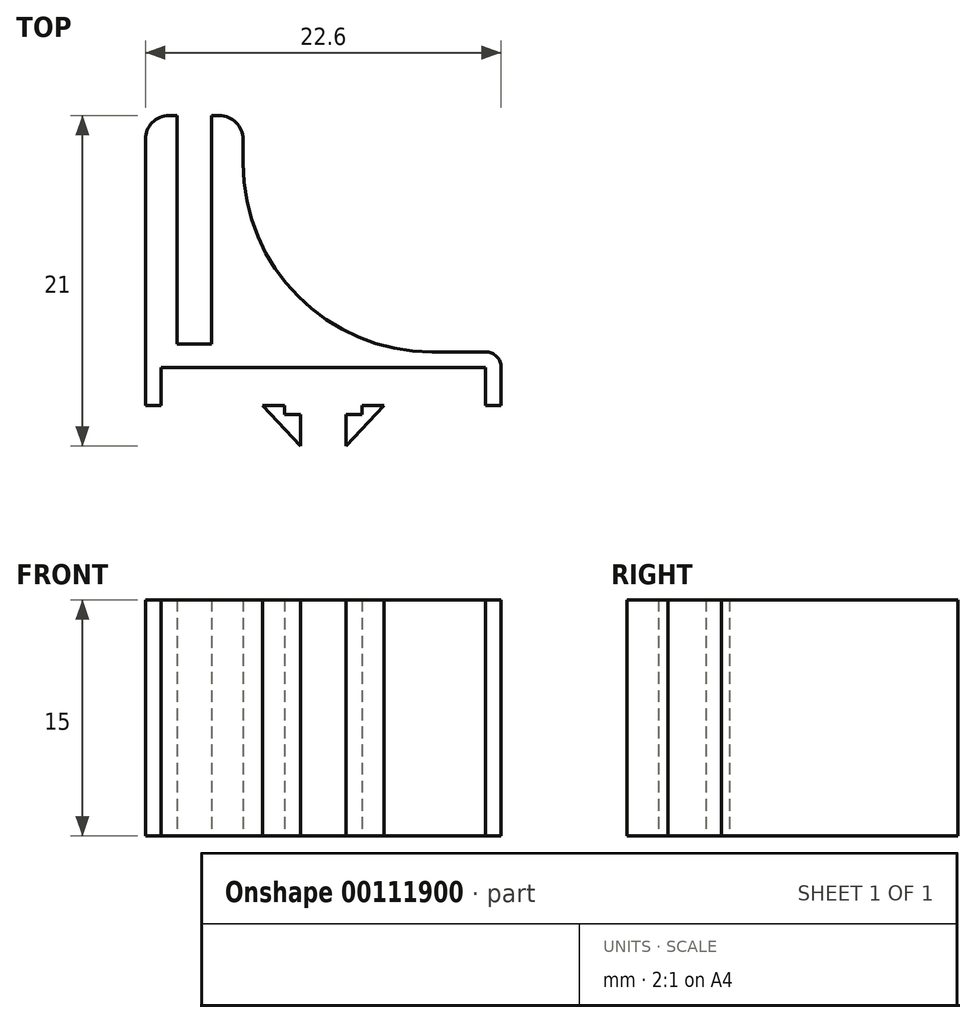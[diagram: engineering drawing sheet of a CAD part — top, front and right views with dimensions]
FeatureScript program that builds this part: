
annotation { "Feature Type Name" : "Feature", "Feature Type Description" : "" }
export const myFeature = defineFeature(function(context is Context, id is Id, definition is map)
    precondition{}
    {
        {
            var Q0;
            Q0=qCreatedBy(makeId("Top.planeOp"),FACE);
            var sketch = newSketch(context, id + "F0", { "sketchPlane" : qUnion([Q0])});
            skLineSegment(sketch, "E0.bottom", {"start": v(-10.3, -5.5) * mm, "end": v(10.3, -5.5) * mm});
            skLineSegment(sketch, "E0.right", {"start": v(10.3, -5.5) * mm, "end": v(10.3, -4.5) * mm});
            skLineSegment(sketch, "E1.bottom", {"start": v(10.3, -5.5) * mm, "end": v(11.3, -5.5) * mm});
            skLineSegment(sketch, "E1.top", {"start": v(10.3, -7.9) * mm, "end": v(11.3, -7.9) * mm});
            skLineSegment(sketch, "E1.left", {"start": v(10.3, -5.5) * mm, "end": v(10.3, -7.9) * mm});
            skLineSegment(sketch, "E1.right", {"start": v(11.3, -5.5) * mm, "end": v(11.3, -7.9) * mm});
            skArc(sketch, "E2", {"start": v(11.3, -5.5) * mm, "mid": v(11, -4.8) * mm, "end": v(10.3, -4.5) * mm});
            skLineSegment(sketch, "E3.bottom", {"start": v(-10.3, -5.5) * mm, "end": v(-11.3, -5.5) * mm});
            skLineSegment(sketch, "E3.top", {"start": v(-10.3, -7.9) * mm, "end": v(-11.3, -7.9) * mm});
            skLineSegment(sketch, "E3.left", {"start": v(-10.3, -5.5) * mm, "end": v(-10.3, -7.9) * mm});
            skLineSegment(sketch, "E3.right", {"start": v(-11.3, -5.5) * mm, "end": v(-11.3, -7.9) * mm});
            skLineSegment(sketch, "E4", {"start": v(-2.45, -5.5) * mm, "end": v(2.45, -5.5) * mm, "construction": true});
            skLineSegment(sketch, "E5.bottom", {"start": v(-2.45, -5.5) * mm, "end": v(-1.45, -5.5) * mm});
            skLineSegment(sketch, "E5.top", {"start": v(-2.45, -8.5) * mm, "end": v(-1.45, -8.5) * mm});
            skLineSegment(sketch, "E5.left", {"start": v(-2.45, -5.5) * mm, "end": v(-2.45, -8.5) * mm});
            skLineSegment(sketch, "E5.right", {"start": v(-1.45, -5.5) * mm, "end": v(-1.45, -8.5) * mm});
            skLineSegment(sketch, "E6.bottom", {"start": v(2.45, -5.5) * mm, "end": v(1.45, -5.5) * mm});
            skLineSegment(sketch, "E6.top", {"start": v(2.45, -8.5) * mm, "end": v(1.45, -8.5) * mm});
            skLineSegment(sketch, "E6.left", {"start": v(2.45, -5.5) * mm, "end": v(2.45, -8.5) * mm});
            skLineSegment(sketch, "E6.right", {"start": v(1.45, -5.5) * mm, "end": v(1.45, -8.5) * mm});
            skLineSegment(sketch, "E7", {"start": v(3.85, -7.9) * mm, "end": v(2.45, -7.9) * mm});
            skLineSegment(sketch, "E8", {"start": v(-2.45, -7.9) * mm, "end": v(-3.85, -7.9) * mm});
            skLineSegment(sketch, "E9", {"start": v(-2.45, -7.9) * mm, "end": v(2.45, -7.9) * mm, "construction": true});
            skLineSegment(sketch, "E10", {"start": v(1.45, -8.5) * mm, "end": v(1.45, -10.5) * mm});
            skLineSegment(sketch, "E11", {"start": v(1.45, -10.5) * mm, "end": v(3.85, -7.9) * mm});
            skLineSegment(sketch, "E12", {"start": v(-1.45, -8.5) * mm, "end": v(-1.45, -10.5) * mm});
            skLineSegment(sketch, "E13", {"start": v(-1.45, -10.5) * mm, "end": v(-3.85, -7.9) * mm});
            skLineSegment(sketch, "E14", {"start": v(-9.3, -4) * mm, "end": v(-7.1, -4) * mm});
            skLineSegment(sketch, "E15", {"start": v(6.9, -4.5) * mm, "end": v(10.3, -4.5) * mm});
            skLineSegment(sketch, "E16", {"start": v(-11.3, -5.5) * mm, "end": v(-11.3, 9) * mm});
            skLineSegment(sketch, "E17", {"start": v(-9.3, -4) * mm, "end": v(-9.3, 10.5) * mm});
            skLineSegment(sketch, "E18", {"start": v(-9.3, 10.5) * mm, "end": v(-9.8, 10.5) * mm});
            skLineSegment(sketch, "E19", {"start": v(-7.1, -4) * mm, "end": v(-7.1, 10.5) * mm});
            skLineSegment(sketch, "E20", {"start": v(-5.1, 7.5) * mm, "end": v(-5.1, 9) * mm});
            skLineSegment(sketch, "E21", {"start": v(-6.6, 10.5) * mm, "end": v(-7.1, 10.5) * mm});
            skLineSegment(sketch, "E22", {"start": v(-9.3, 10.5) * mm, "end": v(-7.1, 10.5) * mm, "construction": true});
            skPoint(sketch, "E23.visualSharp", {"position": v(-11.3, -5.5) * mm});
            skPoint(sketch, "E24.visualSharp", {"position": v(-5.1, -4.5) * mm});
            skArc(sketch, "E24.filletArc", {"start": v(-5.1, 7.5) * mm, "mid": v(-1.59, -0.99) * mm, "end": v(6.9, -4.5) * mm});
            skPoint(sketch, "E25.visualSharp", {"position": v(-11.3, 10.5) * mm});
            skArc(sketch, "E25.filletArc", {"start": v(-9.8, 10.5) * mm, "mid": v(-10.86, 10.06) * mm, "end": v(-11.3, 9) * mm});
            skPoint(sketch, "E26.visualSharp", {"position": v(-5.1, 10.5) * mm});
            skArc(sketch, "E26.filletArc", {"start": v(-5.1, 9) * mm, "mid": v(-5.54, 10.06) * mm, "end": v(-6.6, 10.5) * mm});
            skPoint(sketch, "E27", {"position": v(0, -7.9) * mm});
            skSolve(sketch);
        }
        {
            var Q0;
            Q0=makeQuery(id+"F0.imprint","IMPRINT",FACE,{"disambiguationData":[TD([[makeQuery(id+"F0.imprint","IMPRINT",EDGE,{"derivedFrom":sQuery(id+"F0.wireOp",EDGE,"E1.bottom")}),-1.0]])]});
            var Q1;
            Q1=makeQuery(id+"F0.imprint","IMPRINT",FACE,{"disambiguationData":[TD([[makeQuery(id+"F0.imprint","IMPRINT",EDGE,{"derivedFrom":sQuery(id+"F0.wireOp",EDGE,"E3.bottom")}),1.0]])]});
            var Q2;
            {var subQ1=sQuery(id+"F0.wireOp",EDGE,"E8");Q2=makeQuery(id+"F0.imprint","IMPRINT",FACE,{"disambiguationData":[TD([[makeQuery(id+"F0.imprint","IMPRINT",EDGE,{"derivedFrom":subQ1}),1.0]])]});}
            var Q3;
            {var subQ1=sQuery(id+"F0.wireOp",EDGE,"7c9eb7b9-ca48-4d36-bab2-391d59fa54ff");Q3=makeQuery(id+"F0.imprint","IMPRINT",FACE,{"disambiguationData":[TD([[makeQuery(id+"F0.imprint","IMPRINT",EDGE,{"derivedFrom":subQ1}),-1.0]])]});}
            var Q4;
            Q4=makeQuery(id+"F0.imprint","IMPRINT",FACE,{"disambiguationData":[TD([[makeQuery(id+"F0.imprint","IMPRINT",EDGE,{"derivedFrom":sQuery(id+"F0.wireOp",EDGE,"E0.left")}),1.0]])]});
            var Q5;
            Q5=makeQuery(id+"F0.imprint","IMPRINT",FACE,{"disambiguationData":[TD([[makeQuery(id+"F0.imprint","IMPRINT",EDGE,{"derivedFrom":sQuery(id+"F0.wireOp",EDGE,"E0.right")}),-1.0]])]});
            var Q6;
            {var subQ3=sQuery(id+"F0.wireOp",EDGE,"E5.bottom");Q6=makeQuery(id+"F0.imprint","IMPRINT",FACE,{"disambiguationData":[TD([[makeQuery(id+"F0.imprint","IMPRINT",EDGE,{"derivedFrom":subQ3}),-1.0]])]});}
            var Q7;
            {var subQ2=sQuery(id+"F0.wireOp",EDGE,"E6.bottom");Q7=makeQuery(id+"F0.imprint","IMPRINT",FACE,{"disambiguationData":[TD([[makeQuery(id+"F0.imprint","IMPRINT",EDGE,{"derivedFrom":subQ2}),1.0]])]});}
            var Q8;
            {var subQ0=sQuery(id+"F0.wireOp",EDGE,"7cf5e282-fc27-4f11-9d7e-3bad8ab92ec3");Q8=makeQuery(id+"F0.imprint","IMPRINT",FACE,{"disambiguationData":[TD([[makeQuery(id+"F0.imprint","IMPRINT",EDGE,{"derivedFrom":subQ0}),1.0]])]});}
            var Q9;
            {var subQ0=sQuery(id+"F0.wireOp",EDGE,"9b068b05-5ba9-4f17-919f-f73491ae4f90");Q9=makeQuery(id+"F0.imprint","IMPRINT",FACE,{"disambiguationData":[TD([[makeQuery(id+"F0.imprint","IMPRINT",EDGE,{"derivedFrom":subQ0}),-1.0]])]});}
            var Q10;
            {var subQ1=sQuery(id+"F0.wireOp",EDGE,"E0.left");Q10=makeQuery(id+"F0.imprint","IMPRINT",FACE,{"disambiguationData":[TD([[makeQuery(id+"F0.imprint","IMPRINT",EDGE,{"derivedFrom":subQ1}),-1.0]])]});}
            var Q11;
            {var subQ1=sQuery(id+"F0.wireOp",EDGE,"E0.right");Q11=makeQuery(id+"F0.imprint","IMPRINT",FACE,{"disambiguationData":[TD([[makeQuery(id+"F0.imprint","IMPRINT",EDGE,{"derivedFrom":subQ1}),1.0]])]});}
            var Q12;
            {var subQ0=sQuery(id+"F0.wireOp",EDGE,"E0.top");var subQ2=sQuery(id+"F0.wireOp",EDGE,"ccbefe15-ddc9-4d3c-9180-5a0c61267b28");var subQ4=makeQuery(id+"F0.imprint","INTERSECT",VERTEX,{"disambiguationData":[OD(0.0)],"derivedFrom":[subQ2,subQ0]});Q12=makeQuery(id+"F0.imprint","IMPRINT",FACE,{"disambiguationData":[TD([[makeQuery(id+"F0.imprint","IMPRINT",EDGE,{"disambiguationData":[TD([[subQ4,-1.0]])],"derivedFrom":subQ2}),1.0]])]});}
            var Q13;
            {var subQ2=sQuery(id+"F0.wireOp",EDGE,"E6.top");Q13=makeQuery(id+"F0.imprint","IMPRINT",FACE,{"disambiguationData":[TD([[makeQuery(id+"F0.imprint","IMPRINT",EDGE,{"derivedFrom":subQ2}),1.0]])]});}
            extrude(context, id + "F1", {"entities" : qUnion([Q0, Q1, Q2, Q3, Q4, Q5, Q6, Q7, Q8, Q9, Q10, Q11, Q12, Q13]), "depth" : 15 * mm});
        }
    });
